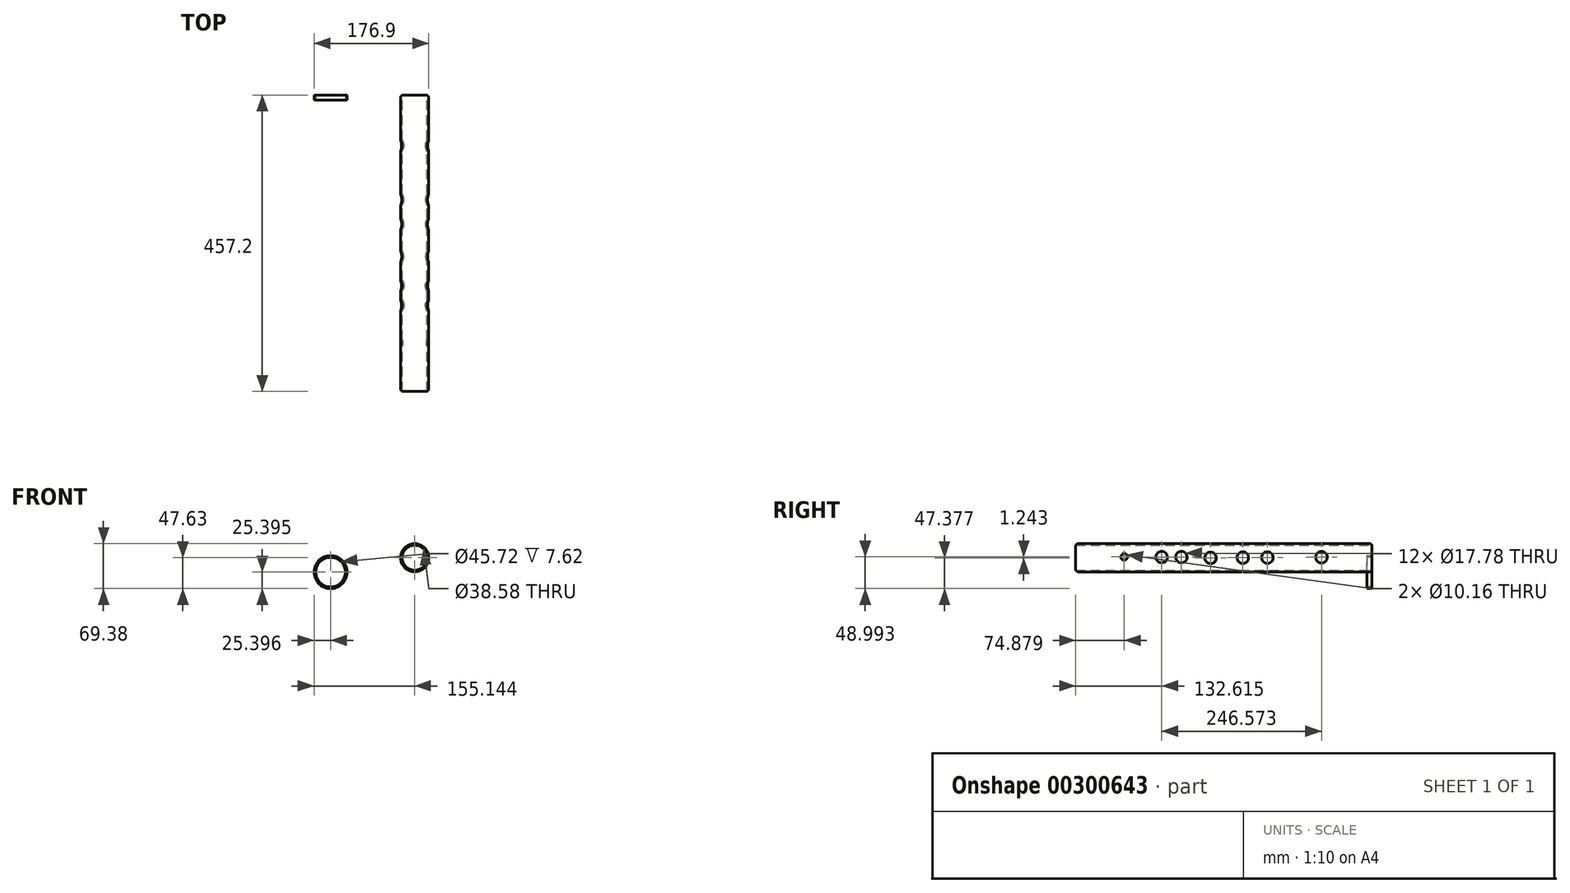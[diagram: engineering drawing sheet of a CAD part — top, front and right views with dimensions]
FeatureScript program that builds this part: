
annotation { "Feature Type Name" : "Feature", "Feature Type Description" : "" }
export const myFeature = defineFeature(function(context is Context, id is Id, definition is map)
    precondition{}
    {
        {
            var Q0;
            Q0=qCreatedBy(makeId("Front.planeOp"),FACE);
            var sketch = newSketch(context, id + "F0", { "sketchPlane" : qUnion([Q0])});
            skCircle(sketch, "E0", {"center": v(-29.66, 11.07) * mm, "radius": 21.75 * mm});
            skSolve(sketch);
        }
        {
            var Q0;
            Q0 = qSketchRegion(id + "F0", true);
            extrude(context, id + "F1", {"entities" : qUnion([Q0]), "depth" : 457.2 * mm});
        }
        {
            var Q0;
            Q0=makeQuery(id+"F1.opExtrude","CAP_FACE",FACE,{"disambiguationData":[OSD([sQuery(id+"F0.wireOp",EDGE,"E0")])],"isStart":false});
            var sketch = newSketch(context, id + "F2", { "sketchPlane" : qUnion([Q0])});
            skSolve(sketch);
        }
        {
            var Q0;
            Q0=qCreatedBy(makeId("Front.planeOp"),FACE);
            var sketch = newSketch(context, id + "F3", { "sketchPlane" : qUnion([Q0])});
            skCircle(sketch, "E1", {"center": v(-159.4, -11.16) * mm, "radius": 25.4 * mm});
            skSolve(sketch);
        }
        {
            var Q0;
            Q0=makeQuery(id+"F3.imprint","IMPRINT",FACE,{"disambiguationData":[TD([[makeQuery(id+"F3.imprint","IMPRINT",EDGE,{"derivedFrom":sQuery(id+"F3.wireOp",EDGE,"E1")}),1.0]])]});
            extrude(context, id + "F4", {"entities" : qUnion([Q0]), "depth" : 7.62 * mm});
        }
        {
            var Q0;
            Q0=makeQuery(id+"F4.opExtrude","CAP_FACE",FACE,{"disambiguationData":[OSD([sQuery(id+"F3.wireOp",EDGE,"E1")])],"isStart":false});
            var sketch = newSketch(context, id + "F5", { "sketchPlane" : qUnion([Q0])});
            skCircle(sketch, "E2", {"center": v(-159.4, -11.16) * mm, "radius": 22.86 * mm});
            skSolve(sketch);
        }
        {
            var Q0;
            Q0=makeQuery(id+"F5.imprint","IMPRINT",FACE,{"disambiguationData":[TD([[makeQuery(id+"F5.imprint","IMPRINT",EDGE,{"derivedFrom":sQuery(id+"F5.wireOp",EDGE,"E2")}),1.0]])]});
            extrude(context, id + "F6", {"entities" : qUnion([Q0]), "operationType" : NewBodyOperationType.REMOVE, "endBound" : BoundingType.THROUGH_ALL, "oppositeDirection" : true, "depth" : 25.4 * mm});
        }
        {
            var Q0;
            Q0=qCreatedBy(makeId("Right.planeOp"),FACE);
            var sketch = newSketch(context, id + "F7", { "sketchPlane" : qUnion([Q0])});
            skCircle(sketch, "E3", {"center": v(-78.01, 11.84) * mm, "radius": 8.9 * mm});
            skCircle(sketch, "E4", {"center": v(-161.5, 11.25) * mm, "radius": 8.9 * mm});
            skCircle(sketch, "E5", {"center": v(-199.38, 11.25) * mm, "radius": 8.9 * mm});
            skCircle(sketch, "E6", {"center": v(-249.2, 10.82) * mm, "radius": 8.9 * mm});
            skCircle(sketch, "E7", {"center": v(-294.1, 12.06) * mm, "radius": 8.9 * mm});
            skCircle(sketch, "E8", {"center": v(-324.58, 12.06) * mm, "radius": 8.9 * mm});
            skCircle(sketch, "E9", {"center": v(-382.32, 12.43) * mm, "radius": 5.08 * mm});
            skSolve(sketch);
        }
        {
            var Q0;
            Q0 = qSketchRegion(id + "F7", true);
            extrude(context, id + "F8", {"entities" : qUnion([Q0]), "operationType" : NewBodyOperationType.REMOVE, "endBound" : BoundingType.THROUGH_ALL, "oppositeDirection" : true, "depth" : 25.4 * mm});
        }
        {
            var Q0;
            Q0=makeQuery(id+"F1.opExtrude","CAP_FACE",FACE,{"disambiguationData":[OSD([sQuery(id+"F0.wireOp",EDGE,"E0")])],"isStart":true});
            var sketch = newSketch(context, id + "F9", { "sketchPlane" : qUnion([Q0])});
            skCircle(sketch, "E10", {"center": v(29.66, 11.07) * mm, "radius": 19.3 * mm});
            skSolve(sketch);
        }
        {
            var Q0;
            Q0=makeQuery(id+"F9.imprint","IMPRINT",FACE,{"disambiguationData":[TD([[makeQuery(id+"F9.imprint","IMPRINT",EDGE,{"derivedFrom":sQuery(id+"F9.wireOp",EDGE,"E10")}),1.0]])]});
            extrude(context, id + "F10", {"entities" : qUnion([Q0]), "operationType" : NewBodyOperationType.REMOVE, "endBound" : BoundingType.THROUGH_ALL, "oppositeDirection" : true, "depth" : 25.4 * mm});
        }
        {
            var Q0;
            Q0=makeQuery(id+"F1.opExtrude","CAP_EDGE",EDGE,{"disambiguationData":[OSD([sQuery(id+"F0.wireOp",EDGE,"E0")])],"isStart":true});
            fillet(context, id + "F11", {"entities" : qUnion([Q0]), "radius" : 5.08 * mm, "tangentPropagation" : true, "allowEdgeOverflow" : false});
        }
        {
            var Q0;
            Q0=makeQuery(id+"F1.opExtrude","CAP_EDGE",EDGE,{"disambiguationData":[OSD([sQuery(id+"F0.wireOp",EDGE,"E0")])],"isStart":false});
            fillet(context, id + "F12", {"entities" : qUnion([Q0]), "radius" : 5.08 * mm, "tangentPropagation" : true, "allowEdgeOverflow" : false});
        }
    });
